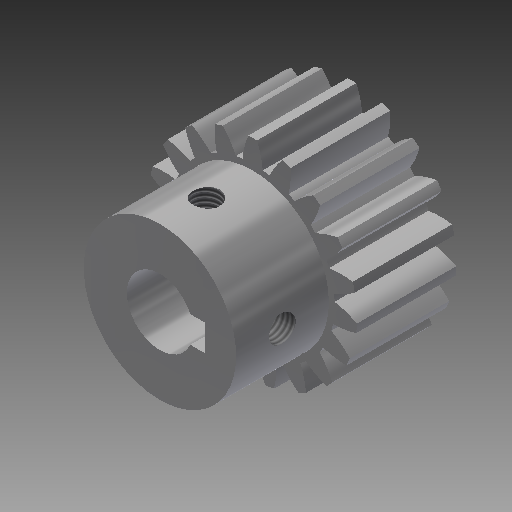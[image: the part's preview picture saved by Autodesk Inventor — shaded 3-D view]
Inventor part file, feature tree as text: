
AUTODESK INVENTOR PART (.ipt)
format: ipt  version: 2019 (Build 230136000, 136)  size: 304,128 bytes
history: native  units: mm (DEFAULTED — no unit token found)
features: sketch x7, extrude x6, plane x5, other x5
ambient origin geometry x8: Origin, YZ Plane, XZ Plane, XY Plane, X Axis, Y Axis, Z Axis, Center Point
bodies: Solid1 (feature_tree)
feature tree (23):
  extrude  "Extrusion1"  Depth=15.0mm TaperAngle=0.0deg
  plane  "Work Plane2"
  plane  "Work Plane8"
  plane  "Work Plane9"
  other  "正齒輪"
  extrude  "擠出2"  Depth=10.0mm TaperAngle=0.0deg
  extrude  "擠出3"  Depth=10.0mm
  extrude  "擠出4"  Depth=10.0mm TaperAngle=0.0deg
  plane  "工作平面11"
  extrude  "擠出5"  TaperAngle=0.0deg  [1 undecoded]
  plane  "工作平面12"
  extrude  "擠出6"  TaperAngle=0.0deg  [1 undecoded]
  other  "螺紋1"
  other  "螺紋2"
  sketch  "Sketch1"  dims[d0=31.5mm d1=15.0mm d2=0.0mm]
  sketch  "Sketch2"  dims[d3=28.5mm d4=10.0mm d5=0.0mm d16=57.0mm d17=0.0mm d34=1.65347mm d39=0.0mm d41=0.0mm d43=57.0mm d46=57.0mm d47=0.0mm d48=0.0mm d49=23.0mm d50=14.0mm d51=0.0mm d52=10.0mm d53=14.0mm d54=0.0mm d57=2.0mm d58=11.8mm d59=14.0mm d60=0.0mm d61=7.0mm d62=4.0mm d63=14.0mm d64=0.0mm d65=7.0mm d66=4.0mm d67=0.0mm d68=0.0mm d69=10.0mm d70=0.0mm d71=10.0mm d72=0.0mm]
  other  "Srf1"
  sketch  "草圖3"
  sketch  "草圖4"
  sketch  "草圖5"
  sketch  "草圖6"
  sketch  "草圖7"
  other  "節圓直徑"
note: 2 required parameter values undecoded (feature->parameter linkage not recoverable at this tier; creation-order binding heuristic only, values carry confidence <= 0.55)
